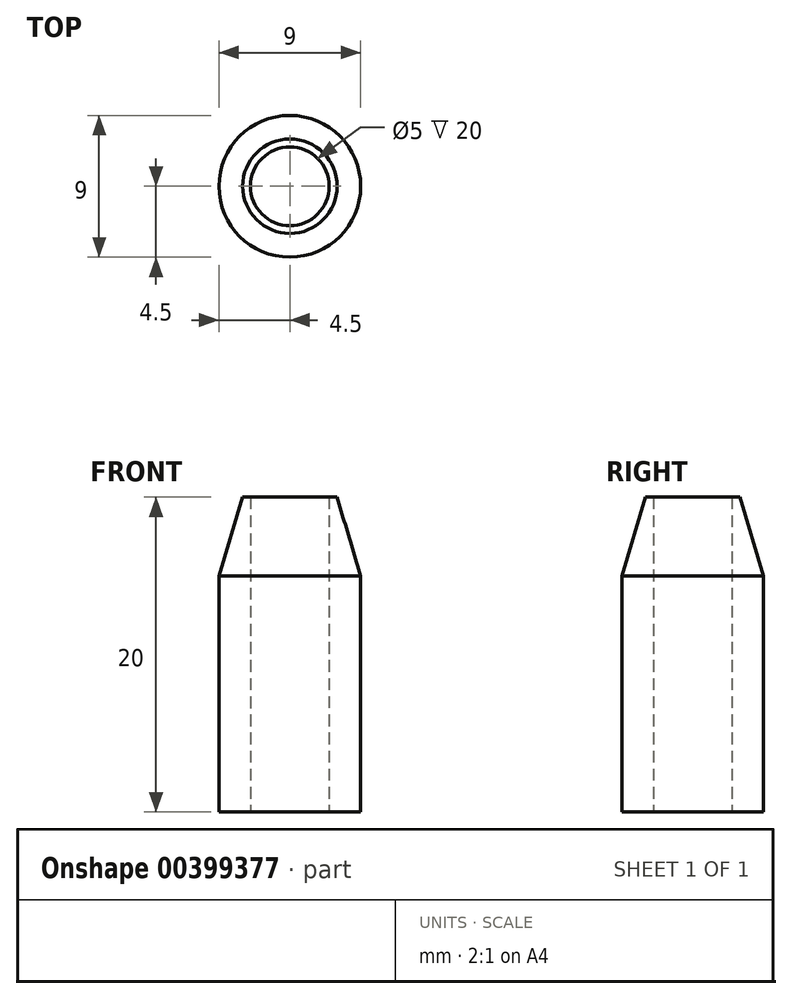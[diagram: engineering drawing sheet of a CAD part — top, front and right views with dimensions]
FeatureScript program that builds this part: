
annotation { "Feature Type Name" : "Feature", "Feature Type Description" : "" }
export const myFeature = defineFeature(function(context is Context, id is Id, definition is map)
    precondition{}
    {
        {
            var Q0;
            Q0=qCreatedBy(makeId("Top.planeOp"),FACE);
            var sketch = newSketch(context, id + "F0", { "sketchPlane" : qUnion([Q0])});
            skCircle(sketch, "E0", {"center": v(0, 0) * mm, "radius": 4.5 * mm});
            skSolve(sketch);
        }
        {
            var Q0;
            Q0=makeQuery(id+"F0.imprint","IMPRINT",FACE,{"disambiguationData":[TD([[makeQuery(id+"F0.imprint","IMPRINT",EDGE,{"derivedFrom":sQuery(id+"F0.wireOp",EDGE,"E0")}),1.0]])]});
            extrude(context, id + "F1", {"entities" : qUnion([Q0]), "depth" : 20 * mm});
        }
        {
            var Q0;
            Q0=makeQuery(id+"F1.opExtrude","CAP_FACE",FACE,{"disambiguationData":[OSD([sQuery(id+"F0.wireOp",EDGE,"E0")])],"isStart":false});
            chamfer(context, id + "F2", {"entities" : qUnion([Q0]), "chamferType" : ChamferType.TWO_OFFSETS, "width1" : 1.5 * mm, "oppositeDirection" : false, "width2" : 5 * mm, "tangentPropagation" : true});
        }
        {
            var Q0;
            Q0=sQuery(id+"F0.wireOp",VERTEX,"E0.center");
            var Q1;
            Q1=makeQuery(id+"F1.opExtrude","SWEPT_BODY",BODY,{"disambiguationData":[OSD([sQuery(id+"F0.wireOp",EDGE,"E0")])]});
            hole(context, id + "F3", {"style" : HoleStyle.SIMPLE, "endStyle" : HoleEndStyle.THROUGH, "oppositeDirection" : true, "holeDiameter" : 5 * mm, "isTappedThrough" : true, "tappedDepth" : 12 * mm, "tapClearance" : 3, "locations" : qUnion([Q0]), "scope" : qUnion([Q1])});
        }
    });
